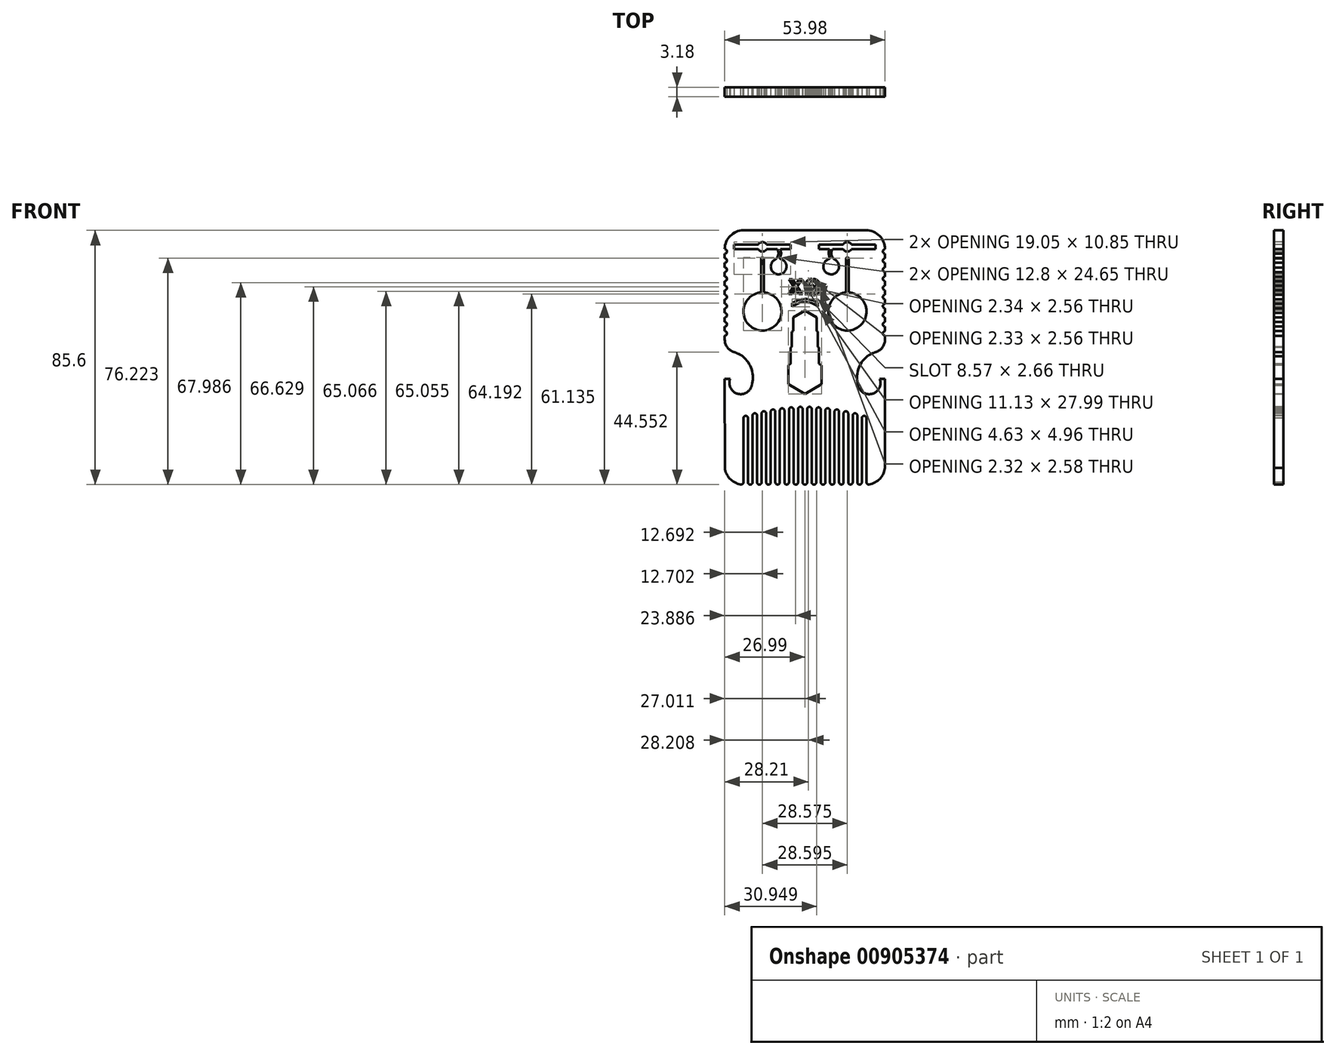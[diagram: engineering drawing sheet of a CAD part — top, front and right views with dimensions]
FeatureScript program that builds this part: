
annotation { "Feature Type Name" : "Feature", "Feature Type Description" : "" }
export const myFeature = defineFeature(function(context is Context, id is Id, definition is map)
    precondition{}
    {
        {
            var Q0;
            Q0=qCreatedBy(makeId("Front.planeOp"),FACE);
            var sketch = newSketch(context, id + "F0", { "sketchPlane" : qUnion([Q0])});
            skLineSegment(sketch, "E0.left", {"start": v(-26.99, 28.82) * mm, "end": v(-26.99, 27.29) * mm});
            skArc(sketch, "E1.filletArc", {"start": v(-20.64, 36.7) * mm, "mid": v(-25.13, 34.84) * mm, "end": v(-26.99, 30.35) * mm});
            skLineSegment(sketch, "E2", {"start": v(-23.81, 30.35) * mm, "end": v(-23.81, 31.94) * mm});
            skLineSegment(sketch, "E3", {"start": v(-23.81, 31.94) * mm, "end": v(-15.89, 31.94) * mm});
            skLineSegment(sketch, "E4", {"start": v(-4.76, 31.94) * mm, "end": v(-4.76, 30.35) * mm});
            skLineSegment(sketch, "E5", {"start": v(-23.81, 30.35) * mm, "end": v(-15.68, 30.35) * mm});
            skLineSegment(sketch, "E6.MirrorCS", {"start": v(-13.53, 19.5) * mm, "end": v(-13.53, 19.5) * mm});
            skLineSegment(sketch, "E7.MirrorCS", {"start": v(-15.06, 19.5) * mm, "end": v(-15.06, 19.5) * mm});
            skLineSegment(sketch, "E8", {"start": v(-13.54, 15.74) * mm, "end": v(-13.53, 15.74) * mm});
            skLineSegment(sketch, "E9.0", {"start": v(-14.75, 27.17) * mm, "end": v(-14.75, 16.35) * mm});
            skLineSegment(sketch, "E10.0", {"start": v(-13.86, 27.17) * mm, "end": v(-13.86, 16.35) * mm});
            skArc(sketch, "E11", {"start": v(-15.3, 15.72) * mm, "mid": v(-14.28, 2.97) * mm, "end": v(-13.32, 15.73) * mm});
            skArc(sketch, "E12", {"start": v(-26.99, 1.23) * mm, "mid": v(-26.23, 2) * mm, "end": v(-26.99, 2.76) * mm});
            skArc(sketch, "E13", {"start": v(-26.99, 4.3) * mm, "mid": v(-26.23, 5.06) * mm, "end": v(-26.99, 5.83) * mm});
            skArc(sketch, "E14", {"start": v(-26.99, 7.36) * mm, "mid": v(-26.23, 8.13) * mm, "end": v(-26.99, 8.9) * mm});
            skArc(sketch, "E15", {"start": v(-26.99, 10.42) * mm, "mid": v(-26.23, 11.2) * mm, "end": v(-26.99, 11.96) * mm});
            skArc(sketch, "E16", {"start": v(-26.99, 13.5) * mm, "mid": v(-26.23, 14.26) * mm, "end": v(-26.99, 15.02) * mm});
            skArc(sketch, "E17", {"start": v(-26.99, 16.56) * mm, "mid": v(-26.23, 17.32) * mm, "end": v(-26.99, 18.09) * mm});
            skArc(sketch, "E18", {"start": v(-26.99, 19.62) * mm, "mid": v(-26.23, 20.39) * mm, "end": v(-26.99, 21.15) * mm});
            skArc(sketch, "E19", {"start": v(-26.99, 22.69) * mm, "mid": v(-26.23, 23.45) * mm, "end": v(-26.99, 24.22) * mm});
            skArc(sketch, "E20", {"start": v(-26.99, 25.75) * mm, "mid": v(-26.23, 26.52) * mm, "end": v(-26.99, 27.29) * mm});
            skArc(sketch, "E21", {"start": v(-26.99, 28.82) * mm, "mid": v(-26.23, 29.59) * mm, "end": v(-26.99, 30.35) * mm});
            skLineSegment(sketch, "E22.trimOffspring", {"start": v(-26.99, 4.3) * mm, "end": v(-26.99, 2.76) * mm});
            skLineSegment(sketch, "E23.trimOffspring", {"start": v(-26.99, 7.36) * mm, "end": v(-26.99, 5.83) * mm});
            skLineSegment(sketch, "E24.trimOffspring", {"start": v(-26.99, 10.42) * mm, "end": v(-26.99, 8.9) * mm});
            skLineSegment(sketch, "E25.trimOffspring", {"start": v(-26.99, 13.5) * mm, "end": v(-26.99, 11.96) * mm});
            skLineSegment(sketch, "E26.trimOffspring", {"start": v(-26.99, 16.56) * mm, "end": v(-26.99, 15.02) * mm});
            skLineSegment(sketch, "E27.trimOffspring", {"start": v(-26.99, 19.62) * mm, "end": v(-26.99, 18.09) * mm});
            skLineSegment(sketch, "E28.trimOffspring", {"start": v(-26.99, 22.69) * mm, "end": v(-26.99, 21.15) * mm});
            skLineSegment(sketch, "E29.trimOffspring", {"start": v(-26.99, 25.75) * mm, "end": v(-26.99, 24.22) * mm});
            skPoint(sketch, "E30.orphan", {"position": v(-14.3, 27.17) * mm});
            skLineSegment(sketch, "E31.trimOffspring", {"start": v(-12.71, 31.94) * mm, "end": v(-4.76, 31.94) * mm});
            skLineSegment(sketch, "E32", {"start": v(-15.89, 31.94) * mm, "end": v(-15.68, 31.94) * mm});
            skArc(sketch, "E33.MirrorCS", {"start": v(-15.68, 31.94) * mm, "mid": v(-14.29, 32.75) * mm, "end": v(-12.9, 31.94) * mm});
            skArc(sketch, "E34.MirrorCS", {"start": v(-12.9, 30.35) * mm, "mid": v(-14.29, 29.55) * mm, "end": v(-15.68, 30.35) * mm});
            skLineSegment(sketch, "E35.trimOffspring", {"start": v(-12.9, 30.35) * mm, "end": v(-9.28, 30.35) * mm});
            skLineSegment(sketch, "E36.trimOffspring", {"start": v(-12.9, 31.94) * mm, "end": v(-12.71, 31.94) * mm});
            skLineSegment(sketch, "E37.trimOffspring", {"start": v(-8.29, 30.35) * mm, "end": v(-4.76, 30.35) * mm});
            skArc(sketch, "E38", {"start": v(-9.9, 26.94) * mm, "mid": v(-8.95, 28.53) * mm, "end": v(-9.28, 30.35) * mm});
            skArc(sketch, "E39.0", {"start": v(-8.4, 27.42) * mm, "mid": v(-8.02, 28.88) * mm, "end": v(-8.29, 30.35) * mm});
            skPoint(sketch, "E40.start.orphan", {"position": v(-9.9, 26.94) * mm});
            skArc(sketch, "E41.MirrorCS", {"start": v(-9.9, 26.94) * mm, "mid": v(-8.58, 21.9) * mm, "end": v(-8.25, 27.1) * mm});
            skPoint(sketch, "E42.orphan", {"position": v(-9.94, 26.92) * mm});
            skArc(sketch, "E43", {"start": v(-15.3, 15.72) * mm, "mid": v(-14.92, 15.94) * mm, "end": v(-14.75, 16.35) * mm});
            skArc(sketch, "E44.MirrorCS", {"start": v(-13.3, 15.72) * mm, "mid": v(-13.69, 15.94) * mm, "end": v(-13.86, 16.35) * mm});
            skArc(sketch, "E45", {"start": v(-8.4, 27.42) * mm, "mid": v(-8.4, 27.23) * mm, "end": v(-8.25, 27.1) * mm});
            skArc(sketch, "E46", {"start": v(-0.77, -48.14) * mm, "mid": v(0, -48.9) * mm, "end": v(0.77, -48.14) * mm});
            skArc(sketch, "E47", {"start": v(2.3, -23.5) * mm, "mid": v(1.53, -22.74) * mm, "end": v(0.77, -23.5) * mm});
            skArc(sketch, "E48.MirrorCS", {"start": v(-26.98, -0.1) * mm, "mid": v(-26.1, -2.7) * mm, "end": v(-23.85, -4.26) * mm});
            skArc(sketch, "E49.MirrorCS", {"start": v(-20.94, -5.71) * mm, "mid": v(-22.34, -4.88) * mm, "end": v(-23.85, -4.26) * mm});
            skArc(sketch, "E50.MirrorCS", {"start": v(-17.92, -15.55) * mm, "mid": v(-17.94, -10.17) * mm, "end": v(-20.94, -5.71) * mm});
            skArc(sketch, "E51.MirrorCS", {"start": v(-25.18, -13.3) * mm, "mid": v(-22.75, -18.29) * mm, "end": v(-17.92, -15.55) * mm});
            skLineSegment(sketch, "E52.MirrorCS", {"start": v(-25.18, -13.3) * mm, "end": v(-26.98, -13.3) * mm});
            skLineSegment(sketch, "E53.MirrorCS", {"start": v(-26.98, -13.3) * mm, "end": v(-26.95, -43.22) * mm});
            skLineSegment(sketch, "E54", {"start": v(-26.98, -0.1) * mm, "end": v(-26.99, 1.23) * mm});
            skArc(sketch, "E55.MirrorCS", {"start": v(20.64, 36.7) * mm, "mid": v(25.13, 34.84) * mm, "end": v(26.99, 30.35) * mm});
            skLineSegment(sketch, "E56.MirrorCS", {"start": v(23.81, 31.94) * mm, "end": v(15.89, 31.94) * mm});
            skArc(sketch, "E57.MirrorCS", {"start": v(15.68, 31.94) * mm, "mid": v(14.29, 32.75) * mm, "end": v(12.9, 31.94) * mm});
            skLineSegment(sketch, "E58.MirrorCS", {"start": v(12.71, 31.94) * mm, "end": v(4.76, 31.94) * mm});
            skLineSegment(sketch, "E59.MirrorCS", {"start": v(4.76, 31.94) * mm, "end": v(4.76, 30.35) * mm});
            skLineSegment(sketch, "E60.MirrorCS", {"start": v(8.29, 30.35) * mm, "end": v(4.76, 30.35) * mm});
            skArc(sketch, "E61.MirrorCS", {"start": v(8.4, 27.42) * mm, "mid": v(8.02, 28.88) * mm, "end": v(8.29, 30.35) * mm});
            skLineSegment(sketch, "E62.MirrorCS", {"start": v(13.86, 27.17) * mm, "end": v(13.86, 16.35) * mm});
            skLineSegment(sketch, "E63.MirrorCS", {"start": v(14.75, 27.17) * mm, "end": v(14.75, 16.35) * mm});
            skLineSegment(sketch, "E64.MirrorCS", {"start": v(12.9, 30.35) * mm, "end": v(9.28, 30.35) * mm});
            skArc(sketch, "E65.MirrorCS", {"start": v(12.9, 30.35) * mm, "mid": v(14.29, 29.55) * mm, "end": v(15.68, 30.35) * mm});
            skLineSegment(sketch, "E66.MirrorCS", {"start": v(23.81, 30.35) * mm, "end": v(15.68, 30.35) * mm});
            skLineSegment(sketch, "E67.MirrorCS", {"start": v(23.81, 30.35) * mm, "end": v(23.81, 31.94) * mm});
            skArc(sketch, "E68.MirrorCS", {"start": v(9.9, 26.94) * mm, "mid": v(8.95, 28.53) * mm, "end": v(9.28, 30.35) * mm});
            skArc(sketch, "E69.MirrorCS", {"start": v(9.9, 26.94) * mm, "mid": v(8.58, 21.9) * mm, "end": v(8.25, 27.1) * mm});
            skArc(sketch, "E70.MirrorCS", {"start": v(8.4, 27.42) * mm, "mid": v(8.4, 27.23) * mm, "end": v(8.25, 27.1) * mm});
            skLineSegment(sketch, "E71.MirrorCS", {"start": v(26.98, -0.1) * mm, "end": v(26.99, 1.23) * mm});
            skArc(sketch, "E72.MirrorCS", {"start": v(26.99, 25.75) * mm, "mid": v(26.23, 26.52) * mm, "end": v(26.99, 27.29) * mm});
            skLineSegment(sketch, "E73.MirrorCS", {"start": v(26.99, 25.75) * mm, "end": v(26.99, 24.22) * mm});
            skArc(sketch, "E74.MirrorCS", {"start": v(26.99, 1.23) * mm, "mid": v(26.23, 2) * mm, "end": v(26.99, 2.76) * mm});
            skArc(sketch, "E75.MirrorCS", {"start": v(26.99, 19.62) * mm, "mid": v(26.23, 20.39) * mm, "end": v(26.99, 21.15) * mm});
            skLineSegment(sketch, "E76.MirrorCS", {"start": v(26.99, 28.82) * mm, "end": v(26.99, 27.29) * mm});
            skLineSegment(sketch, "E77.MirrorCS", {"start": v(26.99, 7.36) * mm, "end": v(26.99, 5.83) * mm});
            skLineSegment(sketch, "E78.MirrorCS", {"start": v(26.99, 16.56) * mm, "end": v(26.99, 15.02) * mm});
            skLineSegment(sketch, "E79.MirrorCS", {"start": v(26.99, 13.5) * mm, "end": v(26.99, 11.96) * mm});
            skLineSegment(sketch, "E80.MirrorCS", {"start": v(26.99, 10.42) * mm, "end": v(26.99, 8.9) * mm});
            skArc(sketch, "E81.MirrorCS", {"start": v(26.99, 22.69) * mm, "mid": v(26.23, 23.45) * mm, "end": v(26.99, 24.22) * mm});
            skArc(sketch, "E82.MirrorCS", {"start": v(26.99, 13.5) * mm, "mid": v(26.23, 14.26) * mm, "end": v(26.99, 15.02) * mm});
            skLineSegment(sketch, "E83.MirrorCS", {"start": v(26.99, 22.69) * mm, "end": v(26.99, 21.15) * mm});
            skArc(sketch, "E84.MirrorCS", {"start": v(26.99, 16.56) * mm, "mid": v(26.23, 17.32) * mm, "end": v(26.99, 18.09) * mm});
            skArc(sketch, "E85.MirrorCS", {"start": v(26.99, 28.82) * mm, "mid": v(26.23, 29.59) * mm, "end": v(26.99, 30.35) * mm});
            skLineSegment(sketch, "E86.MirrorCS", {"start": v(26.99, 4.3) * mm, "end": v(26.99, 2.76) * mm});
            skLineSegment(sketch, "E87.MirrorCS", {"start": v(26.99, 19.62) * mm, "end": v(26.99, 18.09) * mm});
            skArc(sketch, "E88.MirrorCS", {"start": v(26.99, 7.36) * mm, "mid": v(26.23, 8.13) * mm, "end": v(26.99, 8.9) * mm});
            skArc(sketch, "E89.MirrorCS", {"start": v(26.99, 4.3) * mm, "mid": v(26.23, 5.06) * mm, "end": v(26.99, 5.83) * mm});
            skArc(sketch, "E90.MirrorCS", {"start": v(26.99, 10.42) * mm, "mid": v(26.23, 11.2) * mm, "end": v(26.99, 11.96) * mm});
            skArc(sketch, "E91.MirrorCS", {"start": v(13.03, -48.14) * mm, "mid": v(12.26, -48.9) * mm, "end": v(11.5, -48.14) * mm});
            skArc(sketch, "E92.MirrorCS", {"start": v(19.16, -48.14) * mm, "mid": v(18.4, -48.9) * mm, "end": v(17.63, -48.14) * mm});
            skArc(sketch, "E93.MirrorCS", {"start": v(9.96, -48.14) * mm, "mid": v(9.2, -48.9) * mm, "end": v(8.43, -48.14) * mm});
            skArc(sketch, "E94.MirrorCS", {"start": v(6.9, -48.14) * mm, "mid": v(6.13, -48.9) * mm, "end": v(5.37, -48.14) * mm});
            skLineSegment(sketch, "E95.MirrorCS", {"start": v(13.54, 15.74) * mm, "end": v(13.53, 15.74) * mm});
            skArc(sketch, "E96.MirrorCS", {"start": v(0.77, -48.14) * mm, "mid": v(0, -48.9) * mm, "end": v(-0.77, -48.14) * mm});
            skArc(sketch, "E97.MirrorCS", {"start": v(0.77, -23.5) * mm, "mid": v(1.53, -22.74) * mm, "end": v(2.3, -23.5) * mm});
            skArc(sketch, "E98.MirrorCS", {"start": v(13.3, 15.72) * mm, "mid": v(13.69, 15.94) * mm, "end": v(13.86, 16.35) * mm});
            skArc(sketch, "E99.MirrorCS", {"start": v(15.3, 15.72) * mm, "mid": v(14.92, 15.94) * mm, "end": v(14.75, 16.35) * mm});
            skArc(sketch, "E100.MirrorCS", {"start": v(21.63, -48.82) * mm, "mid": v(20.99, -48.68) * mm, "end": v(20.7, -48.09) * mm});
            skLineSegment(sketch, "E101.MirrorCS", {"start": v(12.9, 31.94) * mm, "end": v(12.71, 31.94) * mm});
            skArc(sketch, "E102.MirrorCS", {"start": v(3.83, -48.14) * mm, "mid": v(3.07, -48.9) * mm, "end": v(2.3, -48.14) * mm});
            skLineSegment(sketch, "E103.MirrorCS", {"start": v(15.89, 31.94) * mm, "end": v(15.68, 31.94) * mm});
            skArc(sketch, "E104.MirrorCS", {"start": v(16.1, -48.14) * mm, "mid": v(15.33, -48.9) * mm, "end": v(14.56, -48.14) * mm});
            skLineSegment(sketch, "E105.MirrorCS", {"start": v(25.18, -13.3) * mm, "end": v(26.98, -13.3) * mm});
            skLineSegment(sketch, "E106.MirrorCS", {"start": v(13.53, 19.5) * mm, "end": v(13.53, 19.5) * mm});
            skLineSegment(sketch, "E107.MirrorCS", {"start": v(15.06, 19.5) * mm, "end": v(15.06, 19.5) * mm});
            skArc(sketch, "E108.MirrorCS", {"start": v(20.94, -5.71) * mm, "mid": v(22.34, -4.88) * mm, "end": v(23.85, -4.26) * mm});
            skLineSegment(sketch, "E109.MirrorCS", {"start": v(17.63, -25.66) * mm, "end": v(17.63, -48.14) * mm});
            skLineSegment(sketch, "E110.MirrorCS", {"start": v(11.5, -24.36) * mm, "end": v(11.5, -48.14) * mm});
            skLineSegment(sketch, "E111.MirrorCS", {"start": v(26.98, -13.3) * mm, "end": v(26.95, -43.22) * mm});
            skArc(sketch, "E112.MirrorCS", {"start": v(17.92, -15.55) * mm, "mid": v(17.94, -10.17) * mm, "end": v(20.94, -5.71) * mm});
            skPoint(sketch, "E113.MirrorP", {"position": v(14.3, 27.17) * mm});
            skArc(sketch, "E114.MirrorCS", {"start": v(25.18, -13.3) * mm, "mid": v(22.75, -18.29) * mm, "end": v(17.92, -15.55) * mm});
            skLineSegment(sketch, "E115.MirrorCS", {"start": v(0.77, -48.14) * mm, "end": v(0.77, -23.5) * mm});
            skLineSegment(sketch, "E116.MirrorCS", {"start": v(16.1, -48.14) * mm, "end": v(16.1, -25.66) * mm});
            skPoint(sketch, "E117.MirrorP", {"position": v(9.9, 26.94) * mm});
            skLineSegment(sketch, "E118.MirrorCS", {"start": v(3.83, -48.14) * mm, "end": v(3.83, -23.64) * mm});
            skLineSegment(sketch, "E119.MirrorCS", {"start": v(14.56, -24.94) * mm, "end": v(14.56, -48.14) * mm});
            skArc(sketch, "E120.MirrorCS", {"start": v(15.3, 15.72) * mm, "mid": v(14.28, 2.97) * mm, "end": v(13.32, 15.73) * mm});
            skPoint(sketch, "E121.MirrorP", {"position": v(9.94, 26.92) * mm});
            skArc(sketch, "E122.MirrorCS", {"start": v(26.98, -0.1) * mm, "mid": v(26.1, -2.7) * mm, "end": v(23.85, -4.26) * mm});
            skLineSegment(sketch, "E123.MirrorCS", {"start": v(5.37, -23.64) * mm, "end": v(5.37, -48.14) * mm});
            skLineSegment(sketch, "E124.MirrorCS", {"start": v(13.03, -48.14) * mm, "end": v(13.03, -24.94) * mm});
            skLineSegment(sketch, "E125.MirrorCS", {"start": v(19.16, -48.14) * mm, "end": v(19.16, -26.52) * mm});
            skLineSegment(sketch, "E126.MirrorCS", {"start": v(9.96, -48.14) * mm, "end": v(9.96, -24.36) * mm});
            skLineSegment(sketch, "E127.MirrorCS", {"start": v(8.43, -23.95) * mm, "end": v(8.43, -48.14) * mm});
            skLineSegment(sketch, "E128.MirrorCS", {"start": v(2.3, -23.5) * mm, "end": v(2.3, -48.14) * mm});
            skLineSegment(sketch, "E129.MirrorCS", {"start": v(6.9, -48.14) * mm, "end": v(6.9, -23.95) * mm});
            skLineSegment(sketch, "E130", {"start": v(-20.64, 36.7) * mm, "end": v(20.64, 36.7) * mm});
            skArc(sketch, "E131", {"start": v(4.3, 12.31) * mm, "mid": v(0, 13.56) * mm, "end": v(-4.26, 12.19) * mm});
            skArc(sketch, "E132", {"start": v(1.59, 18.98) * mm, "mid": v(1.34, 18.42) * mm, "end": v(1.22, 17.81) * mm});
            skArc(sketch, "E133", {"start": v(1.32, 16.84) * mm, "mid": v(1.68, 16.15) * mm, "end": v(2.39, 15.82) * mm});
            skArc(sketch, "E134", {"start": v(2.38, 20.36) * mm, "mid": v(2.03, 20.33) * mm, "end": v(1.69, 20.25) * mm});
            skArc(sketch, "E135", {"start": v(1.69, 20.25) * mm, "mid": v(1.26, 20.08) * mm, "end": v(0.88, 19.82) * mm});
            skArc(sketch, "E136", {"start": v(0.88, 19.82) * mm, "mid": v(0.52, 19.43) * mm, "end": v(0.28, 18.96) * mm});
            skArc(sketch, "E137", {"start": v(0.28, 18.96) * mm, "mid": v(0.11, 18.4) * mm, "end": v(0.05, 17.81) * mm});
            skArc(sketch, "E138", {"start": v(0.05, 17.81) * mm, "mid": v(0.05, 17.8) * mm, "end": v(0.05, 17.8) * mm});
            skArc(sketch, "E139", {"start": v(0.09, 17) * mm, "mid": v(0.16, 16.62) * mm, "end": v(0.28, 16.25) * mm});
            skArc(sketch, "E140", {"start": v(0.28, 16.25) * mm, "mid": v(0.42, 15.96) * mm, "end": v(0.6, 15.7) * mm});
            skArc(sketch, "E141", {"start": v(0.6, 15.7) * mm, "mid": v(0.86, 15.43) * mm, "end": v(1.16, 15.21) * mm});
            skArc(sketch, "E142", {"start": v(1.16, 15.21) * mm, "mid": v(1.5, 15.05) * mm, "end": v(1.87, 14.94) * mm});
            skArc(sketch, "E143", {"start": v(1.87, 14.94) * mm, "mid": v(2.1, 14.9) * mm, "end": v(2.35, 14.88) * mm});
            skArc(sketch, "E144", {"start": v(2.35, 14.88) * mm, "mid": v(2.37, 14.88) * mm, "end": v(2.39, 14.88) * mm});
            skLineSegment(sketch, "E145", {"start": v(2.58, 19.42) * mm, "end": v(2.58, 19.42) * mm});
            skLineSegment(sketch, "E146", {"start": v(2.59, 15.81) * mm, "end": v(2.59, 15.8) * mm});
            skLineSegment(sketch, "E147.trimOffspring", {"start": v(2.39, 19.4) * mm, "end": v(2.38, 20.37) * mm});
            skLineSegment(sketch, "E148", {"start": v(2.39, 15.35) * mm, "end": v(2.39, 14.88) * mm});
            skArc(sketch, "E149.trimOffspring", {"start": v(2.59, 14.87) * mm, "mid": v(2.6, 14.87) * mm, "end": v(2.6, 14.87) * mm});
            skLineSegment(sketch, "E150.trimOffspring", {"start": v(2.39, 15.82) * mm, "end": v(2.39, 15.35) * mm});
            skArc(sketch, "E151.trimOffspring", {"start": v(2.39, 19.4) * mm, "mid": v(1.95, 19.26) * mm, "end": v(1.59, 18.98) * mm});
            skPoint(sketch, "E152.orphan", {"position": v(1.21, 17.55) * mm});
            skArc(sketch, "E153.MirrorCS", {"start": v(2.77, 19.4) * mm, "mid": v(3.2, 19.26) * mm, "end": v(3.57, 18.99) * mm});
            skArc(sketch, "E154.MirrorCS", {"start": v(3.57, 18.99) * mm, "mid": v(3.82, 18.43) * mm, "end": v(3.94, 17.83) * mm});
            skArc(sketch, "E155.MirrorCS", {"start": v(3.86, 16.85) * mm, "mid": v(3.5, 16.16) * mm, "end": v(2.8, 15.82) * mm});
            skArc(sketch, "E156.MirrorCS", {"start": v(2.85, 14.88) * mm, "mid": v(2.83, 14.88) * mm, "end": v(2.8, 14.88) * mm});
            skArc(sketch, "E157.MirrorCS", {"start": v(3.32, 14.95) * mm, "mid": v(3.09, 14.9) * mm, "end": v(2.85, 14.88) * mm});
            skArc(sketch, "E158.MirrorCS", {"start": v(4.03, 15.22) * mm, "mid": v(3.69, 15.06) * mm, "end": v(3.32, 14.95) * mm});
            skArc(sketch, "E159.MirrorCS", {"start": v(4.58, 15.71) * mm, "mid": v(4.33, 15.44) * mm, "end": v(4.03, 15.22) * mm});
            skArc(sketch, "E160.MirrorCS", {"start": v(4.9, 16.27) * mm, "mid": v(4.76, 15.98) * mm, "end": v(4.58, 15.71) * mm});
            skArc(sketch, "E161.MirrorCS", {"start": v(5.08, 17.02) * mm, "mid": v(5.02, 16.64) * mm, "end": v(4.9, 16.27) * mm});
            skArc(sketch, "E162.MirrorCS", {"start": v(5.11, 17.84) * mm, "mid": v(5.11, 17.83) * mm, "end": v(5.11, 17.83) * mm});
            skArc(sketch, "E163.MirrorCS", {"start": v(4.88, 18.98) * mm, "mid": v(5.05, 18.42) * mm, "end": v(5.11, 17.84) * mm});
            skArc(sketch, "E164.MirrorCS", {"start": v(4.27, 19.84) * mm, "mid": v(4.63, 19.45) * mm, "end": v(4.88, 18.98) * mm});
            skArc(sketch, "E165.MirrorCS", {"start": v(3.45, 20.26) * mm, "mid": v(3.88, 20.1) * mm, "end": v(4.27, 19.84) * mm});
            skArc(sketch, "E166.MirrorCS", {"start": v(2.76, 20.37) * mm, "mid": v(3.11, 20.33) * mm, "end": v(3.45, 20.26) * mm});
            skLineSegment(sketch, "E167.MirrorCS", {"start": v(2.77, 19.4) * mm, "end": v(2.76, 20.37) * mm});
            skLineSegment(sketch, "E168.MirrorCS", {"start": v(2.8, 15.82) * mm, "end": v(2.8, 15.35) * mm});
            skLineSegment(sketch, "E169.MirrorCS", {"start": v(2.8, 15.35) * mm, "end": v(2.8, 14.88) * mm});
            skArc(sketch, "E170", {"start": v(2.59, 15.8) * mm, "mid": v(2.6, 15.8) * mm, "end": v(2.6, 15.8) * mm});
            skLineSegment(sketch, "E171.0", {"start": v(0.05, 17.43) * mm, "end": v(1.22, 17.43) * mm});
            skLineSegment(sketch, "E172.0", {"start": v(0.05, 17.8) * mm, "end": v(1.22, 17.81) * mm});
            skLineSegment(sketch, "E173.trimOffspring", {"start": v(3.94, 17.83) * mm, "end": v(5.12, 17.83) * mm});
            skPoint(sketch, "E174.orphan", {"position": v(2.58, 17.62) * mm});
            skLineSegment(sketch, "E175.trimOffspring", {"start": v(3.95, 17.45) * mm, "end": v(5.12, 17.45) * mm});
            skPoint(sketch, "E176.MirrorCS.end.orphan", {"position": v(2.6, 15.8) * mm});
            skPoint(sketch, "E176.MirrorCS.start.orphan", {"position": v(2.8, 15.82) * mm});
            skPoint(sketch, "E177.MirrorCS.end.orphan", {"position": v(2.98, 14.87) * mm});
            skPoint(sketch, "E177.MirrorCS.start.orphan", {"position": v(3.19, 14.88) * mm});
            skPoint(sketch, "E178.orphan", {"position": v(2.57, 20.37) * mm});
            skPoint(sketch, "E179.MirrorCS.end.orphan", {"position": v(2.77, 19.4) * mm});
            skArc(sketch, "E180.trimOffspring", {"start": v(0.05, 17.43) * mm, "mid": v(0.06, 17.21) * mm, "end": v(0.09, 17) * mm});
            skArc(sketch, "E181.trimOffspring", {"start": v(1.22, 17.43) * mm, "mid": v(1.25, 17.13) * mm, "end": v(1.32, 16.84) * mm});
            skArc(sketch, "E182.trimOffspring", {"start": v(3.95, 17.45) * mm, "mid": v(3.92, 17.15) * mm, "end": v(3.86, 16.85) * mm});
            skArc(sketch, "E183.trimOffspring", {"start": v(5.12, 17.45) * mm, "mid": v(5.1, 17.24) * mm, "end": v(5.08, 17.02) * mm});
            skText(sketch, "E184", { "text": "X", "fontName": "OpenSans-Bold.ttf"});
            skLineSegment(sketch, "E185", {"start": v(4.3, 11.06) * mm, "end": v(4.3, 12.31) * mm});
            skLineSegment(sketch, "E186", {"start": v(4.3, 12.31) * mm, "end": v(4.3, 11.06) * mm});
            skCircle(sketch, "E187", {"center": v(2.58, 17.62) * mm, "radius": 0.65 * mm});
            skArc(sketch, "E188.0", {"start": v(4.3, 11.06) * mm, "mid": v(0, 12.55) * mm, "end": v(-4.26, 10.9) * mm});
            skLineSegment(sketch, "E189", {"start": v(-4.26, 12.19) * mm, "end": v(-4.26, 10.9) * mm});
            skLineSegment(sketch, "E190.trimOffspring", {"start": v(20.7, -26.52) * mm, "end": v(20.7, -48.09) * mm});
            skArc(sketch, "E191.MirrorCS", {"start": v(3.83, -23.64) * mm, "mid": v(4.6, -22.89) * mm, "end": v(5.37, -23.64) * mm});
            skArc(sketch, "E192.MirrorCS", {"start": v(9.96, -24.36) * mm, "mid": v(10.73, -23.6) * mm, "end": v(11.5, -24.36) * mm});
            skArc(sketch, "E193.MirrorCS", {"start": v(19.16, -26.52) * mm, "mid": v(19.93, -25.76) * mm, "end": v(20.7, -26.52) * mm});
            skArc(sketch, "E194.MirrorCS", {"start": v(16.1, -25.66) * mm, "mid": v(16.86, -24.9) * mm, "end": v(17.63, -25.66) * mm});
            skArc(sketch, "E195.MirrorCS", {"start": v(13.03, -24.94) * mm, "mid": v(13.8, -24.19) * mm, "end": v(14.56, -24.94) * mm});
            skArc(sketch, "E196.MirrorCS", {"start": v(6.9, -23.95) * mm, "mid": v(7.66, -23.2) * mm, "end": v(8.43, -23.95) * mm});
            skArc(sketch, "E197.MirrorCS", {"start": v(-13.03, -24.94) * mm, "mid": v(-13.8, -24.19) * mm, "end": v(-14.56, -24.94) * mm});
            skArc(sketch, "E198.MirrorCS", {"start": v(-19.16, -26.52) * mm, "mid": v(-19.93, -25.76) * mm, "end": v(-20.7, -26.52) * mm});
            skArc(sketch, "E199.MirrorCS", {"start": v(-13.03, -48.14) * mm, "mid": v(-12.26, -48.9) * mm, "end": v(-11.5, -48.14) * mm});
            skArc(sketch, "E200.MirrorCS", {"start": v(-19.16, -48.14) * mm, "mid": v(-18.4, -48.9) * mm, "end": v(-17.63, -48.14) * mm});
            skArc(sketch, "E201.MirrorCS", {"start": v(-2.3, -23.5) * mm, "mid": v(-1.53, -22.74) * mm, "end": v(-0.77, -23.5) * mm});
            skLineSegment(sketch, "E202.MirrorCS", {"start": v(-20.7, -26.52) * mm, "end": v(-20.7, -48.09) * mm});
            skLineSegment(sketch, "E203.MirrorCS", {"start": v(-14.56, -24.94) * mm, "end": v(-14.56, -48.14) * mm});
            skLineSegment(sketch, "E204.MirrorCS", {"start": v(-8.43, -23.95) * mm, "end": v(-8.43, -48.14) * mm});
            skLineSegment(sketch, "E205.MirrorCS", {"start": v(-5.37, -23.64) * mm, "end": v(-5.37, -48.14) * mm});
            skLineSegment(sketch, "E206.MirrorCS", {"start": v(-0.77, -48.14) * mm, "end": v(-0.77, -23.5) * mm});
            skArc(sketch, "E207.MirrorCS", {"start": v(-9.96, -24.36) * mm, "mid": v(-10.73, -23.6) * mm, "end": v(-11.5, -24.36) * mm});
            skLineSegment(sketch, "E208.MirrorCS", {"start": v(-2.3, -23.5) * mm, "end": v(-2.3, -48.14) * mm});
            skArc(sketch, "E209.MirrorCS", {"start": v(-0.77, -23.5) * mm, "mid": v(-1.53, -22.74) * mm, "end": v(-2.3, -23.5) * mm});
            skLineSegment(sketch, "E210.MirrorCS", {"start": v(-11.5, -24.36) * mm, "end": v(-11.5, -48.14) * mm});
            skLineSegment(sketch, "E211.MirrorCS", {"start": v(-19.16, -48.14) * mm, "end": v(-19.16, -26.52) * mm});
            skArc(sketch, "E212.MirrorCS", {"start": v(-16.1, -48.14) * mm, "mid": v(-15.33, -48.9) * mm, "end": v(-14.56, -48.14) * mm});
            skLineSegment(sketch, "E213.MirrorCS", {"start": v(-13.03, -48.14) * mm, "end": v(-13.03, -24.94) * mm});
            skArc(sketch, "E214.MirrorCS", {"start": v(-6.9, -48.14) * mm, "mid": v(-6.13, -48.9) * mm, "end": v(-5.37, -48.14) * mm});
            skLineSegment(sketch, "E215.MirrorCS", {"start": v(-16.1, -48.14) * mm, "end": v(-16.1, -25.66) * mm});
            skArc(sketch, "E216.MirrorCS", {"start": v(-3.83, -48.14) * mm, "mid": v(-3.07, -48.9) * mm, "end": v(-2.3, -48.14) * mm});
            skLineSegment(sketch, "E217.MirrorCS", {"start": v(-9.96, -48.14) * mm, "end": v(-9.96, -24.36) * mm});
            skLineSegment(sketch, "E218.MirrorCS", {"start": v(-3.83, -48.14) * mm, "end": v(-3.83, -23.64) * mm});
            skLineSegment(sketch, "E219.MirrorCS", {"start": v(-6.9, -48.14) * mm, "end": v(-6.9, -23.95) * mm});
            skArc(sketch, "E220.MirrorCS", {"start": v(-3.83, -23.64) * mm, "mid": v(-4.6, -22.89) * mm, "end": v(-5.37, -23.64) * mm});
            skLineSegment(sketch, "E221.MirrorCS", {"start": v(-17.63, -25.66) * mm, "end": v(-17.63, -48.14) * mm});
            skArc(sketch, "E222.MirrorCS", {"start": v(-21.63, -48.82) * mm, "mid": v(-20.99, -48.68) * mm, "end": v(-20.7, -48.09) * mm});
            skArc(sketch, "E223.MirrorCS", {"start": v(-9.96, -48.14) * mm, "mid": v(-9.2, -48.9) * mm, "end": v(-8.43, -48.14) * mm});
            skArc(sketch, "E224.MirrorCS", {"start": v(-16.1, -25.66) * mm, "mid": v(-16.86, -24.9) * mm, "end": v(-17.63, -25.66) * mm});
            skArc(sketch, "E225.MirrorCS", {"start": v(-6.9, -23.95) * mm, "mid": v(-7.66, -23.2) * mm, "end": v(-8.43, -23.95) * mm});
            skArc(sketch, "E226", {"start": v(-26.95, -43.22) * mm, "mid": v(-25.24, -46.92) * mm, "end": v(-21.63, -48.82) * mm});
            skLineSegment(sketch, "E227.MirrorCS", {"start": v(23.59, -46.44) * mm, "end": v(23.59, -46.44) * mm});
            skArc(sketch, "E228.MirrorCS", {"start": v(26.95, -43.22) * mm, "mid": v(25.24, -46.92) * mm, "end": v(21.63, -48.82) * mm});
            skLineSegment(sketch, "E229.0", {"start": v(5.56, -8.71) * mm, "end": v(5.56, -15.13) * mm});
            skLineSegment(sketch, "E229.3", {"start": v(-5.56, -15.13) * mm, "end": v(-5.56, -8.71) * mm});
            skLineSegment(sketch, "E229.4", {"start": v(-5.56, -8.71) * mm, "end": v(-4.76, -8.25) * mm});
            skLineSegment(sketch, "E229.5", {"start": v(4.76, -8.25) * mm, "end": v(5.56, -8.71) * mm});
            skPoint(sketch, "E229.0.midPoint", {"position": v(5.56, -11.92) * mm});
            skLineSegment(sketch, "E230.0", {"start": v(4.76, -2.75) * mm, "end": v(4.76, -8.25) * mm});
            skLineSegment(sketch, "E230.3", {"start": v(-4.76, -8.25) * mm, "end": v(-4.76, -2.75) * mm});
            skLineSegment(sketch, "E230.4", {"start": v(-4.76, -2.75) * mm, "end": v(-4.38, -2.53) * mm});
            skLineSegment(sketch, "E230.5", {"start": v(4.38, -2.53) * mm, "end": v(4.76, -2.75) * mm});
            skPoint(sketch, "E230.0.midPoint", {"position": v(4.76, -5.5) * mm});
            skLineSegment(sketch, "E231.0", {"start": v(4.38, 2.53) * mm, "end": v(4.38, -2.53) * mm});
            skLineSegment(sketch, "E231.3", {"start": v(-4.38, -2.53) * mm, "end": v(-4.38, 2.53) * mm});
            skLineSegment(sketch, "E231.4", {"start": v(-4.38, 2.53) * mm, "end": v(-3.98, 2.76) * mm});
            skLineSegment(sketch, "E231.5", {"start": v(3.98, 2.76) * mm, "end": v(4.38, 2.53) * mm});
            skPoint(sketch, "E231.0.midPoint", {"position": v(4.38, 0) * mm});
            skLineSegment(sketch, "E232.4", {"start": v(5.56, -15.13) * mm, "end": v(0, -18.35) * mm});
            skLineSegment(sketch, "E232.5", {"start": v(0, -18.35) * mm, "end": v(-5.56, -15.13) * mm});
            skPoint(sketch, "E232.0.midPoint", {"position": v(-5.56, -11.92) * mm});
            skLineSegment(sketch, "E233.0", {"start": v(-3.98, 2.76) * mm, "end": v(-3.98, 7.35) * mm});
            skLineSegment(sketch, "E233.1", {"start": v(-3.98, 7.35) * mm, "end": v(0, 9.65) * mm});
            skLineSegment(sketch, "E233.2", {"start": v(0, 9.65) * mm, "end": v(3.98, 7.35) * mm});
            skLineSegment(sketch, "E233.3", {"start": v(3.98, 7.35) * mm, "end": v(3.98, 2.76) * mm});
            skPoint(sketch, "E233.0.midPoint", {"position": v(-3.98, 5.06) * mm});
            skArc(sketch, "E234", {"start": v(-13.86, 27.17) * mm, "mid": v(-14.3, 27.62) * mm, "end": v(-14.75, 27.17) * mm});
            skArc(sketch, "E235", {"start": v(14.75, 27.17) * mm, "mid": v(14.3, 27.62) * mm, "end": v(13.86, 27.17) * mm});
            skArc(sketch, "E236.MirrorCS", {"start": v(-137.62, -2.2) * mm, "mid": v(-138.39, -1.45) * mm, "end": v(-139.16, -2.2) * mm});
            skArc(sketch, "E237.MirrorCS", {"start": v(-137.62, -23.82) * mm, "mid": v(-136.86, -24.58) * mm, "end": v(-136.09, -23.82) * mm});
            skLineSegment(sketch, "E238.MirrorCS", {"start": v(-139.16, -2.2) * mm, "end": v(-139.16, -23.77) * mm});
            skLineSegment(sketch, "E239.MirrorCS", {"start": v(-137.62, -23.82) * mm, "end": v(-137.62, -2.2) * mm});
            skLineSegment(sketch, "E240.MirrorCS", {"start": v(-134.56, -23.82) * mm, "end": v(-134.56, -1.34) * mm});
            skLineSegment(sketch, "E241.MirrorCS", {"start": v(-136.09, -1.34) * mm, "end": v(-136.09, -23.82) * mm});
            skArc(sketch, "E242.MirrorCS", {"start": v(-140.1, -24.5) * mm, "mid": v(-139.45, -24.36) * mm, "end": v(-139.16, -23.77) * mm});
            skArc(sketch, "E243.MirrorCS", {"start": v(-134.56, -1.34) * mm, "mid": v(-135.32, -0.58) * mm, "end": v(-136.09, -1.34) * mm});
            const initialGuessF0  = {"E184": [-0.00542, 0.01525, 1, 0, 0.005]};
            skSetInitialGuess(sketch, initialGuessF0);
            skSolve(sketch);
        }
        {
            var Q0;
            Q0=makeQuery(id+"F0.imprint","IMPRINT",FACE,{"disambiguationData":[TD([[makeQuery(id+"F0.imprint","IMPRINT",EDGE,{"derivedFrom":sQuery(id+"F0.wireOp",EDGE,"945780b4-efe2-4a2c-96a2-a7884967cd02.0")}),1.0]])]});
            var Q1;
            Q1=makeQuery(id+"F0.imprint","IMPRINT",FACE,{"disambiguationData":[TD([[makeQuery(id+"F0.imprint","IMPRINT",EDGE,{"derivedFrom":sQuery(id+"F0.wireOp",EDGE,"E0.left")}),1.0]])]});
            extrude(context, id + "F1", {"entities" : qUnion([Q0, Q1]), "oppositeDirection" : true, "depth" : 3.17 * mm, "offsetDistance" : 25.4 * mm});
        }
    });
